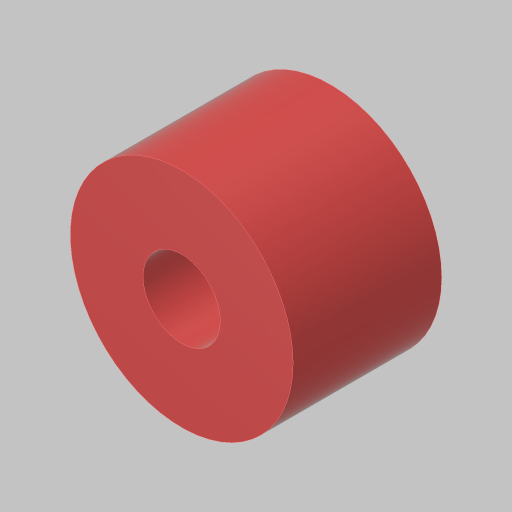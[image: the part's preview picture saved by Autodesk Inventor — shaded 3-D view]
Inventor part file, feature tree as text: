
AUTODESK INVENTOR PART (.ipt)
format: ipt  version: 2023.5 (Build 275446000, 446)  size: 109,568 bytes
history: native  units: in
note: dims shown in document units (in); Inventor stores cm internally (conversion verified against a paired STEP export)
features: extrude x1, sketch x1
ambient origin geometry x8: Origin, YZ Plane, XZ Plane, XY Plane, X Axis, Y Axis, Z Axis, Center Point
bodies: Solid1 (feature_tree)
feature tree (2):
  extrude  "Extrusion1"  Depth=0.5in
  sketch  "Sketch1"  dims[d0=0.75in d1=0.26in d2=0.5in d3=0.0in]
